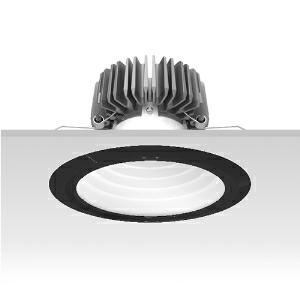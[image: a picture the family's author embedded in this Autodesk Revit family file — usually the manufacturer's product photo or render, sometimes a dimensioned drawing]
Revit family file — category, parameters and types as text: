
# Revit family: 3f_filippi_-_3f_reno_bianco_ampio_3f_filippi_-_30687_a01026_-_3f_reno_200_wh_4000-840_dali_wide___vt_bk_2c67
name_source: partatom
category: Lighting Fixtures
units: mm (PartAtom-declared; Revit-internal decimal feet)

## family parameters
Cut with Voids When Loaded = No
Host = Face
Light Source = No
Part Type = Normal
Room Calculation Point = No
Round Connector Dimension = Use Diameter
Shared = No

## types (1)
- 3F Filippi - 3F Reno Bianco Ampio (1 x LED, 3379 lm, 36 W, 4000 K)
    Apparent Load = 36 VA
    Approval mark = CE
    CIE Flux Codes = 75 94 99 100 100
    Color Rendering = 80
    Color Temperature = 4000 K
    Control Gear = Electronic transformer
    Default Elevation = 1800 mm
    Description = ILLUMINOTECHNICAL
Luminous efficiency 100% (DLOR 100%, ULOR 0%).
Initial luminous flux of the luminaire 3379 lm.
Direct symmetric wide distribution.
Installation Interdistance Transv.D = 1.56 x hu - Long.D = 1.56 x hu.
Tabular UGR (CIE 117 - 4H-8H; S=0.25H; 70/50/20): RUG 22.8 - 22.7.
Beam angle: 74° - 74°.
Luminous efficacy 94 lm/W.
Lifetime (L90/B10): 30000 h. (tq+25°C)
Lifetime (L85/B10): 50000 h. (tq+25°C)
Lifetime (L70/B10): 80000 h. (tq+25°C)
Sudden decreased luminous flux after 50000 hours: 0% (C0).
Photobiological safety in compliance with IEC/TR 62778: RG1 low risk, (IEC 62471).
In compliance with IEC/EN 62722-2-1 - IEC/EN 62717 standards.

SOURCE
Compact LED module 4000/840.
Energy efficiency class (UE 2019/2020 - UE 2019/2015): D.
CIE 13.3 Colour rendering index: CRI >80 (R9 <50%).
IES TM-30 Fidelity Index: Rf = 84 Rg = 95.
CCT nominal colour temperature 4000 K.
Colour initial tolerance (MacAdam): SDCM 3.
Zhaga Book 3 compliant.

MECHANICAL
Passive heat dissipator in die-casting aluminium, oversized, for optimum thermal management of the LED module.
Parabolic element with graduated/concentric rings in white polycarbonate.
Transparent external lens with glossy and satin differentiated surfaces, with a cooling and anti-insect system in methacrylate (PMMA).
Fastening spring clips in stainless steel.
Dimensions: diameter 226 mm, height 146 mm. Weight 1.76 kg.
IP44 protection degree for exposed part, IP20 for recessed part.
Mechanical strength to impacts IK06 (1 joule).
Glow-wire test resistance 650°C.

ELECTRICAL
Wiring on a separate unit.
Halogen Free DALI-2 DATI (Parts 251, 252, 253), PUSH-DIM, electronic wiring 230V-50/60Hz, power factor 0.97 at full load, THD <25%, constant output current, SELV, class II, 1 driver, 1 DALI addresse.
Power of the luminaire 36 W.
ENEC - CE.
SAFE FLICKER: PstLM=<1 and SVM=<0.4 (IEC TR 61547-1 and IEC TR 63158), to ensure a more comfortable and safe light.
Luminaire compliant with EN 60598-2-22 for power supply from a centralised emergency system CPSS (Central Power Supply System), not incorporated in the luminaire - high risk areas excluded. The default power and flux are 100% in AC and 100% in DC.
Ambient temperature from 0°C to +25°C.
Temperature class T6 max 85°C.
Relative humidity UR: <85%.

INSTALLATION
Pull-up recessed fitting.
False ceiling carving: 200 mm.
All accessories dedicated to this product are available on the Catalog and on our website www.3F-Filippi.com.

ACCESSORIES
A01026 - VT transparent glass, tempered, not flammable, locked and in line with the trim, in black polycarbonate.

APPLICATIONS
Environments: architectural, commercial, exhibition areas, transit areas, corridors, shops, display windows, service areas.
In false ceilings with narrow voids.

LIGHT MANAGEMENT
Recommended minimum setting: 10%.
The luminaire, equipped with (DALI-2 DATI) driver, can be controlled manually with 3F Easy Dim technology or automatically/manually with wired or wireless DALI/D2D control systems.
The D2D driver guarantees interoperability with other devices with the same certification by making the following information available:
Device Data (Part 251), Energy Report (Part 252), Diagnosis & Maintenance (Part 253).
In electrical systems without a regulation system (manual or automatic) and DALI bus, a suitable jumper must be made on the DA-DA terminals of the appliance.

WARNING
Luminaire designed for disposal/recycling at end-of-life.
Replaceable (LED only) light source by a professional. Replaceable control gear by a professional.
    Height = 0 mm  [stored 0 ft]
    Lamp = 1 x LED
    Lamp Light Flux = 3379 lm
    Lamp Power = 36 W
    Lamp count = 1
    Length = 226 mm
    Lifetime = 50000 h
    Luminous efficacy = 94 lm/W
    Manufacturer = 3F Filippi
    ModVariant = No
    Model = 3F Filippi - 30687+A01026 - 3F Reno 200 WH 4000-840 DALI WIDE + VT BK
    Mounting Place = Ceiling
    Mounting Type = Recessed
    Number of Poles = 1
    OnlyDefault = Yes
    Power Factor = 1
    Product Name = 3F Filippi - 3F Reno Bianco Ampio
    Product group = recessed luminaire
    ProductGroupID = 4
    Protection Class = Protection class II
    Protection Degree = IP 20
    RLX_Detail_Level = 1
    RLX_Emergency_Light_Flux = 0 lm
    RLX_Emergency_Type = 0
    RLX_Emergency_Type_DB = No
    RlxData = <blob elided: 102521 chars, md5=d338e307>
    Socket = socket
    Standby Power = 0 W
    System Light Flux = 3379 lm
    System Power = 36 W
    Type Comments = Product without accessories
    Type Image = 3ffilippi_3f_reno_200_wh__a01026.jpg
    URL = http://relux.com
    VarID = ---
    Voltage = 0 V
    Weight = 0.00 kg
    Width = 0 mm  [stored 0 ft]

note: [stored X ft] marks values corroborated as IEEE doubles in the binary element streams (Revit-internal decimal feet)

## geometry (parser evidence)
native form markers: Blend x4, Sweep x11
no freeform markers — native parametric forms only
